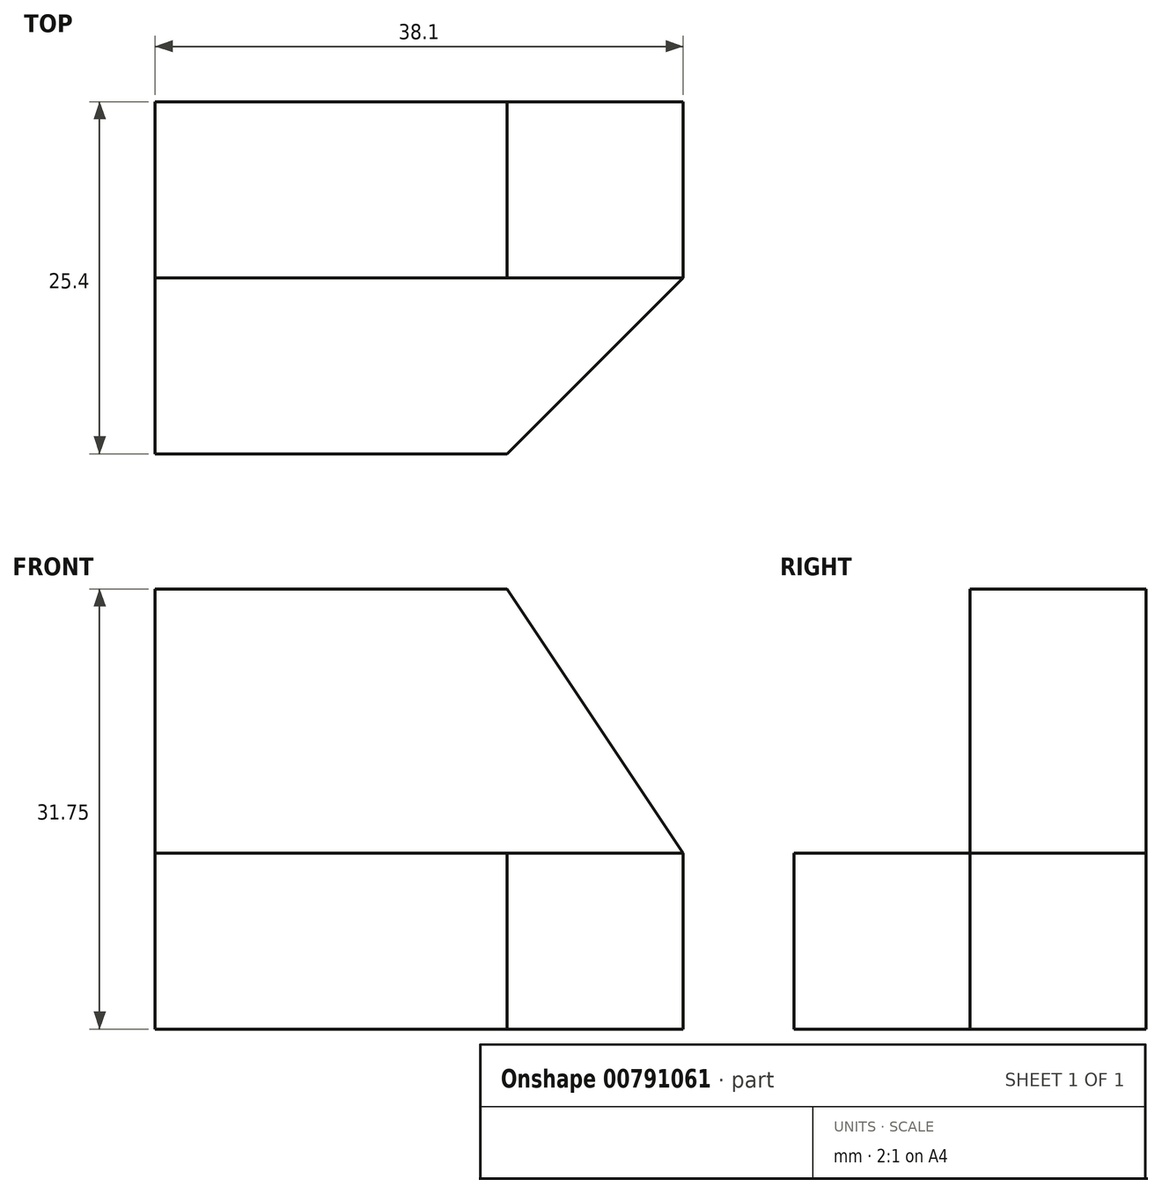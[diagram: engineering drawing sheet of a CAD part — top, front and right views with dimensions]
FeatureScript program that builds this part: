
annotation { "Feature Type Name" : "Feature", "Feature Type Description" : "" }
export const myFeature = defineFeature(function(context is Context, id is Id, definition is map)
    precondition{}
    {
        {
            var Q0;
            Q0=qCreatedBy(makeId("Right.planeOp"),FACE);
            var sketch = newSketch(context, id + "F0", { "sketchPlane" : qUnion([Q0])});
            skLineSegment(sketch, "E0", {"start": v(0, 0) * mm, "end": v(25.4, 0) * mm});
            skLineSegment(sketch, "E1", {"start": v(25.4, 0) * mm, "end": v(25.4, 31.75) * mm});
            skLineSegment(sketch, "E2", {"start": v(25.4, 31.75) * mm, "end": v(12.7, 31.75) * mm});
            skLineSegment(sketch, "E3", {"start": v(0, 0) * mm, "end": v(0, 12.7) * mm});
            skLineSegment(sketch, "E4", {"start": v(0, 12.7) * mm, "end": v(12.7, 12.7) * mm});
            skLineSegment(sketch, "E5", {"start": v(12.7, 12.7) * mm, "end": v(12.7, 31.75) * mm});
            skSolve(sketch);
        }
        {
            var Q0;
            Q0 = qSketchRegion(id + "F0", true);
            extrude(context, id + "F1", {"entities" : qUnion([Q0]), "depth" : 38.1 * mm, "offsetDistance" : 25.4 * mm});
        }
        {
            var Q0;
            Q0=makeQuery(id+"F1.opExtrude","SWEPT_FACE",FACE,{"disambiguationData":[OSD([sQuery(id+"F0.wireOp",EDGE,"E4")])]});
            var sketch = newSketch(context, id + "F2", { "sketchPlane" : qUnion([Q0])});
            skLineSegment(sketch, "E6", {"start": v(25.4, 0) * mm, "end": v(38.1, 12.7) * mm});
            skLineSegment(sketch, "E7", {"start": v(38.1, 12.7) * mm, "end": v(38.1, 0) * mm});
            skLineSegment(sketch, "E8", {"start": v(25.4, 0) * mm, "end": v(38.1, 0) * mm});
            skSolve(sketch);
        }
        {
            var Q0;
            Q0=makeQuery(id+"F2.imprint","IMPRINT",FACE,{"disambiguationData":[TD([[makeQuery(id+"F2.imprint","IMPRINT",EDGE,{"derivedFrom":sQuery(id+"F2.wireOp",EDGE,"E6")}),-1.0]])]});
            extrude(context, id + "F3", {"entities" : qUnion([Q0]), "operationType" : NewBodyOperationType.REMOVE, "oppositeDirection" : true, "depth" : 25.4 * mm, "offsetDistance" : 25.4 * mm});
        }
        {
            var Q0;
            Q0=makeQuery(id+"F1.opExtrude","SWEPT_FACE",FACE,{"disambiguationData":[OSD([sQuery(id+"F0.wireOp",EDGE,"E5")])]});
            var sketch = newSketch(context, id + "F4", { "sketchPlane" : qUnion([Q0])});
            skLineSegment(sketch, "E9", {"start": v(25.4, 31.75) * mm, "end": v(38.1, 12.7) * mm});
            skLineSegment(sketch, "E10", {"start": v(38.1, 12.7) * mm, "end": v(38.1, 31.75) * mm});
            skLineSegment(sketch, "E11", {"start": v(38.1, 31.75) * mm, "end": v(25.4, 31.75) * mm});
            skSolve(sketch);
        }
        {
            var Q0;
            Q0=makeQuery(id+"F4.imprint","IMPRINT",FACE,{"disambiguationData":[TD([[makeQuery(id+"F4.imprint","IMPRINT",EDGE,{"derivedFrom":sQuery(id+"F4.wireOp",EDGE,"E9")}),1.0]])]});
            extrude(context, id + "F5", {"entities" : qUnion([Q0]), "operationType" : NewBodyOperationType.REMOVE, "endBound" : BoundingType.THROUGH_ALL, "oppositeDirection" : true, "depth" : 12.7 * mm, "offsetDistance" : 25.4 * mm});
        }
    });
